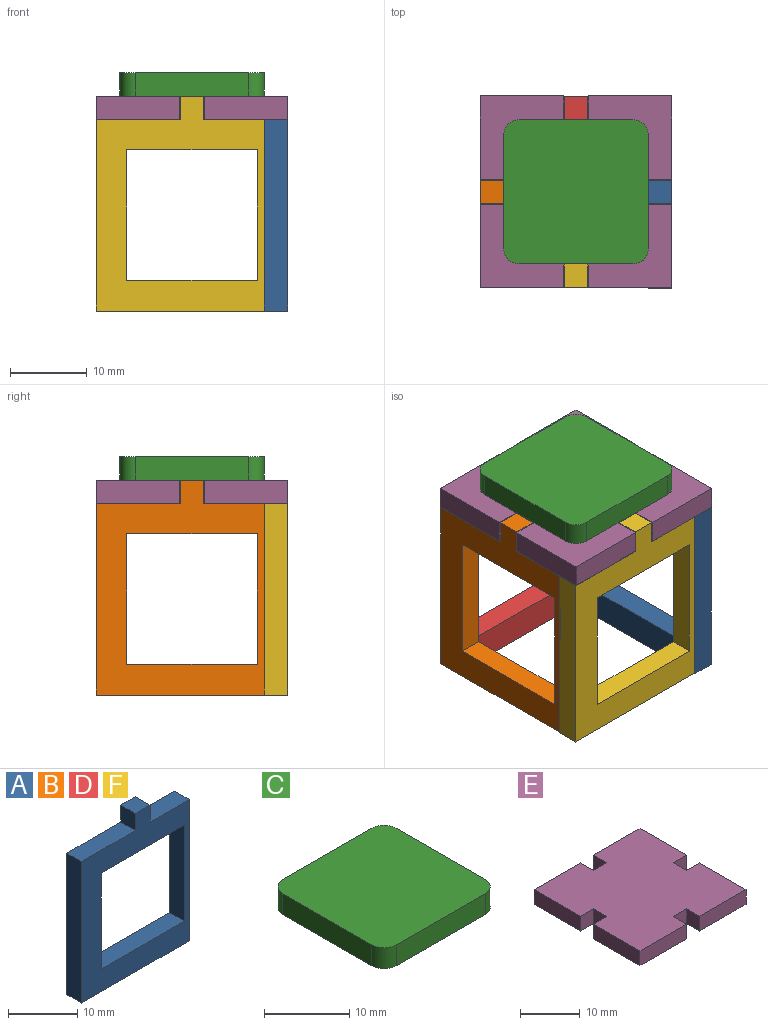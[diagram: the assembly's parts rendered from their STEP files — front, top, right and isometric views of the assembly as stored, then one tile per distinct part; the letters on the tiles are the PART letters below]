
ASSEMBLY  parts=6 mates=5
PART A: 14 faces, bbox 22x3x28 mm
  f0: plane 28x22mm, normal (0,-1,0), area 270mm2, adj f2,f3,f4,f5,f6,f7,f8,f9
  f1: plane 28x22mm, normal (0,1,0), area 270mm2, adj f2,f3,f4,f5,f6,f7,f8,f9
  f2: plane 17x3mm, normal (-1,0,0), area 51mm2, adj f0,f1,f3,f12
  f3: plane 17x3mm, normal (0,0,1), area 51mm2, adj f0,f1,f2,f4
  f4: plane 17x3mm, normal (1,0,0), area 51mm2, adj f0,f1,f3,f12
  f5: plane 3x3mm, normal (0,0,1), area 9mm2, adj f0,f1,f6,f11
  f6: plane 3x3mm, normal (-1,0,0), area 9mm2, adj f0,f1,f5,f7
  f7: plane 11x3mm, normal (0,0,1), area 33mm2, adj f0,f1,f6,f8
  f8: plane 25x3mm, normal (-1,0,0), area 75mm2, adj f0,f1,f7,f9
  f9: plane 22x3mm, normal (0,0,-1), area 66mm2, adj f0,f1,f8,f13
  f10: plane 8x3mm, normal (0,0,1), area 24mm2, adj f0,f1,f11,f13
  f11: plane 3x3mm, normal (1,0,0), area 9mm2, adj f0,f1,f5,f10
  f12: plane 17x3mm, normal (0,0,-1), area 51mm2, adj f0,f1,f2,f4
  f13: plane 25x3mm, normal (1,0,0), area 75mm2, adj f0,f1,f9,f10
PART B: same geometry as A
PART C: 10 faces, bbox 18.8x18.8x3 mm
  f0: plane 14.8x3mm, normal (-1,0,0), area 44.4mm2, adj f4,f5,f6,f9
  f1: plane 14.8x3mm, normal (0,-1,0), area 44.4mm2, adj f4,f5,f6,f7
  f2: plane 14.8x3mm, normal (1,0,0), area 44.4mm2, adj f4,f5,f7,f8
  f3: plane 14.8x3mm, normal (0,1,0), area 44.4mm2, adj f4,f5,f8,f9
  f4: plane 18.8x18.8mm, normal (0,0,1), area 350mm2, adj f0,f1,f2,f3,f6,f7,f8,f9
  f5: plane 18.8x18.8mm, normal (0,0,-1), area 350mm2, adj f0,f1,f2,f3,f6,f7,f8,f9
  f6: cylinder r=2mm len=3mm, axis (0,0,1), area 9.4mm2, adj f0,f1,f4,f5
  f7: cylinder r=2mm len=3mm, axis (0,0,-1), area 9.4mm2, adj f1,f2,f4,f5
  f8: cylinder r=2mm len=3mm, axis (0,0,1), area 9.4mm2, adj f2,f3,f4,f5
  f9: cylinder r=2mm len=3mm, axis (0,0,-1), area 9.4mm2, adj f0,f3,f4,f5
PART D: same geometry as A
PART E: 22 faces, bbox 25x25x3 mm
  f0: plane 10.9x3mm, normal (-1,0,0), area 32.7mm2, adj f1,f19,f20,f21
  f1: plane 10.9x3mm, normal (0,-1,0), area 32.7mm2, adj f0,f2,f20,f21
  f2: plane 3.1x3mm, normal (1,0,0), area 9.3mm2, adj f1,f3,f20,f21
  f3: plane 3.2x3mm, normal (0,-1,0), area 9.6mm2, adj f2,f4,f20,f21
  f4: plane 3.1x3mm, normal (-1,0,0), area 9.3mm2, adj f3,f5,f20,f21
  f5: plane 10.9x3mm, normal (0,-1,0), area 32.7mm2, adj f4,f6,f20,f21
  f6: plane 10.9x3mm, normal (1,0,0), area 32.7mm2, adj f5,f7,f20,f21
  f7: plane 3.1x3mm, normal (0,1,0), area 9.3mm2, adj f6,f8,f20,f21
  f8: plane 3.2x3mm, normal (1,0,0), area 9.6mm2, adj f7,f9,f20,f21
  f9: plane 3.1x3mm, normal (0,-1,0), area 9.3mm2, adj f8,f10,f20,f21
  f10: plane 10.9x3mm, normal (1,0,0), area 32.7mm2, adj f9,f11,f20,f21
  f11: plane 10.9x3mm, normal (0,1,0), area 32.7mm2, adj f10,f12,f20,f21
  f12: plane 3.1x3mm, normal (-1,0,0), area 9.3mm2, adj f11,f13,f20,f21
  f13: plane 3.2x3mm, normal (0,1,0), area 9.6mm2, adj f12,f14,f20,f21
  f14: plane 3.1x3mm, normal (1,0,0), area 9.3mm2, adj f13,f15,f20,f21
  f15: plane 10.9x3mm, normal (0,1,0), area 32.7mm2, adj f14,f16,f20,f21
  f16: plane 10.9x3mm, normal (-1,0,0), area 32.7mm2, adj f15,f17,f20,f21
  f17: plane 3.1x3mm, normal (0,-1,0), area 9.3mm2, adj f16,f18,f20,f21
  f18: plane 3.2x3mm, normal (-1,0,0), area 9.6mm2, adj f17,f19,f20,f21
  f19: plane 3.1x3mm, normal (0,1,0), area 9.3mm2, adj f0,f18,f20,f21
  f20: plane 25x25mm, normal (0,0,1), area 585.3mm2, adj f0,f1,f2,f3,f4,f5,f6,f7
  f21: plane 25x25mm, normal (0,0,-1), area 585.3mm2, adj f0,f1,f2,f3,f4,f5,f6,f7
PART F: same geometry as A
PLACE A rot(axis=(0,0,1),90deg) t=(3.32,10.39,-28.82)mm
PLACE B rot(axis=(0,0,-1),90deg) t=(-15.48,-14.61,-28.82)mm
PLACE C t=(-6.08,-2.11,-0.82)mm
PLACE D rot(axis=(0,0,1),180deg) t=(-18.58,7.29,-28.82)mm
PLACE E t=(-6.08,-2.11,-3.82)mm
PLACE F t=(6.42,-11.51,-28.82)mm
MATE cylindrical D.f1 <-> E.f13  axis (0,-1,0) through (-6.08,7.29,-0.82)mm
MATE cylindrical A.f1 <-> E.f8  axis (-1,0,0) through (3.32,-2.11,-0.82)mm
MATE cylindrical E.f3 <-> F.f1  axis (0,-1,0) through (-6.08,-11.51,-0.82)mm
MATE cylindrical B.f1 <-> E.f18  axis (1,0,0) through (-15.48,-2.11,-0.82)mm
MATE planar C.f5 <-> E.f20  axis (0,0,-1) through (-6.08,-2.11,-0.82)mm
